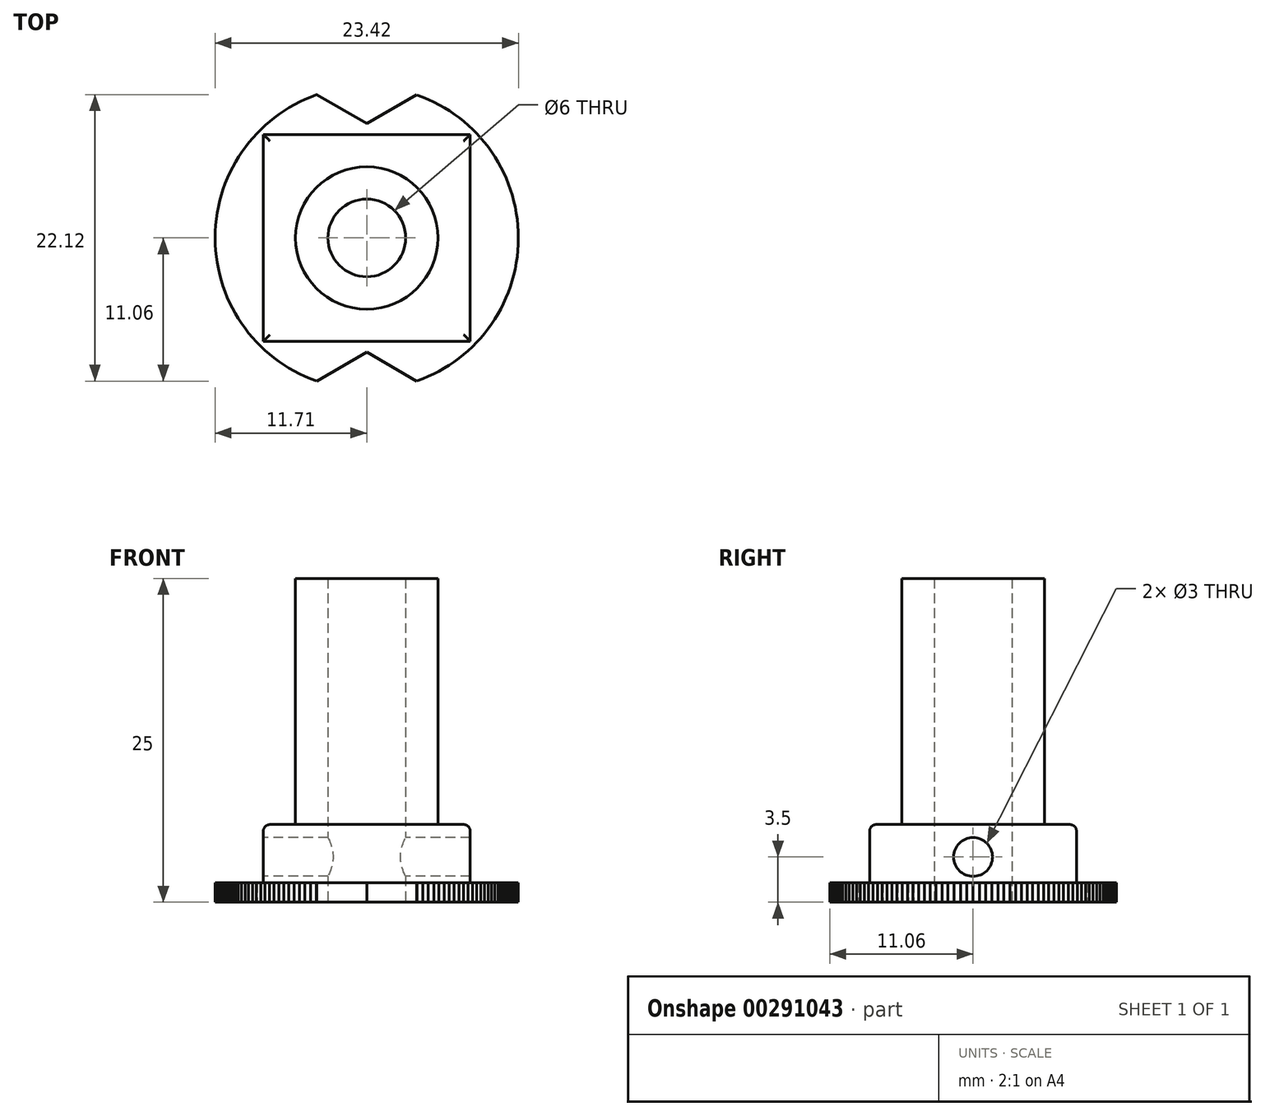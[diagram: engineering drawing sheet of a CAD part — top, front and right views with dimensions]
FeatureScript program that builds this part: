
annotation { "Feature Type Name" : "Feature", "Feature Type Description" : "" }
export const myFeature = defineFeature(function(context is Context, id is Id, definition is map)
    precondition{}
    {
        {
            var Q0;
            Q0=qCreatedBy(makeId("Top.planeOp"),FACE);
            var sketch = newSketch(context, id + "F0", { "sketchPlane" : qUnion([Q0])});
            skLineSegment(sketch, "E0", {"start": v(7.98, 7.98) * mm, "end": v(-7.98, 7.98) * mm});
            skLineSegment(sketch, "E1", {"start": v(-7.98, 7.98) * mm, "end": v(-7.98, -7.99) * mm});
            skLineSegment(sketch, "E2", {"start": v(-7.98, -7.99) * mm, "end": v(7.98, -7.99) * mm});
            skLineSegment(sketch, "E3", {"start": v(7.98, -7.99) * mm, "end": v(7.98, 7.98) * mm});
            skLineSegment(sketch, "E4", {"start": v(11.36, 2.84) * mm, "end": v(11.24, 3.3) * mm});
            skLineSegment(sketch, "E5", {"start": v(11.24, 3.3) * mm, "end": v(11.1, 3.74) * mm});
            skLineSegment(sketch, "E6", {"start": v(11.1, 3.74) * mm, "end": v(10.94, 4.17) * mm});
            skLineSegment(sketch, "E7", {"start": v(10.94, 4.17) * mm, "end": v(10.77, 4.6) * mm});
            skLineSegment(sketch, "E8", {"start": v(10.77, 4.6) * mm, "end": v(10.58, 5.02) * mm});
            skLineSegment(sketch, "E9", {"start": v(10.58, 5.02) * mm, "end": v(10.37, 5.44) * mm});
            skLineSegment(sketch, "E10", {"start": v(10.37, 5.44) * mm, "end": v(10.15, 5.84) * mm});
            skLineSegment(sketch, "E11", {"start": v(10.15, 5.84) * mm, "end": v(9.91, 6.23) * mm});
            skLineSegment(sketch, "E12", {"start": v(9.91, 6.23) * mm, "end": v(9.66, 6.62) * mm});
            skLineSegment(sketch, "E13", {"start": v(9.66, 6.62) * mm, "end": v(9.4, 6.99) * mm});
            skLineSegment(sketch, "E14", {"start": v(9.4, 6.99) * mm, "end": v(9.11, 7.35) * mm});
            skLineSegment(sketch, "E15", {"start": v(9.11, 7.35) * mm, "end": v(8.82, 7.7) * mm});
            skLineSegment(sketch, "E16", {"start": v(8.82, 7.7) * mm, "end": v(8.5, 8.04) * mm});
            skLineSegment(sketch, "E17", {"start": v(8.5, 8.04) * mm, "end": v(8.19, 8.37) * mm});
            skLineSegment(sketch, "E18", {"start": v(8.19, 8.37) * mm, "end": v(7.85, 8.68) * mm});
            skLineSegment(sketch, "E19", {"start": v(7.85, 8.68) * mm, "end": v(7.5, 8.98) * mm});
            skLineSegment(sketch, "E20", {"start": v(7.5, 8.98) * mm, "end": v(7.15, 9.27) * mm});
            skLineSegment(sketch, "E21", {"start": v(7.15, 9.27) * mm, "end": v(6.78, 9.55) * mm});
            skLineSegment(sketch, "E22", {"start": v(6.78, 9.55) * mm, "end": v(6.4, 9.8) * mm});
            skLineSegment(sketch, "E23", {"start": v(6.4, 9.8) * mm, "end": v(6, 10.05) * mm});
            skLineSegment(sketch, "E24", {"start": v(6, 10.05) * mm, "end": v(5.6, 10.28) * mm});
            skLineSegment(sketch, "E25", {"start": v(5.6, 10.28) * mm, "end": v(5.2, 10.5) * mm});
            skLineSegment(sketch, "E26", {"start": v(5.2, 10.5) * mm, "end": v(4.77, 10.7) * mm});
            skLineSegment(sketch, "E27", {"start": v(4.77, 10.7) * mm, "end": v(4.34, 10.88) * mm});
            skLineSegment(sketch, "E28", {"start": v(4.34, 10.88) * mm, "end": v(3.9, 11.04) * mm});
            skLineSegment(sketch, "E29", {"start": v(3.9, 11.04) * mm, "end": v(3.85, 11.06) * mm});
            skLineSegment(sketch, "E30", {"start": v(3.85, 11.06) * mm, "end": v(0, 8.83) * mm});
            skLineSegment(sketch, "E31", {"start": v(0, 8.83) * mm, "end": v(-3.85, 11.06) * mm});
            skLineSegment(sketch, "E32", {"start": v(-3.85, 11.06) * mm, "end": v(-3.89, 11.04) * mm});
            skLineSegment(sketch, "E33", {"start": v(-3.89, 11.04) * mm, "end": v(-4.32, 10.88) * mm});
            skLineSegment(sketch, "E34", {"start": v(-4.32, 10.88) * mm, "end": v(-4.75, 10.7) * mm});
            skLineSegment(sketch, "E35", {"start": v(-4.75, 10.7) * mm, "end": v(-5.17, 10.5) * mm});
            skLineSegment(sketch, "E36", {"start": v(-5.17, 10.5) * mm, "end": v(-5.58, 10.3) * mm});
            skLineSegment(sketch, "E37", {"start": v(-5.58, 10.3) * mm, "end": v(-5.98, 10.06) * mm});
            skLineSegment(sketch, "E38", {"start": v(-5.98, 10.06) * mm, "end": v(-6.37, 9.82) * mm});
            skLineSegment(sketch, "E39", {"start": v(-6.37, 9.82) * mm, "end": v(-6.75, 9.56) * mm});
            skLineSegment(sketch, "E40", {"start": v(-6.75, 9.56) * mm, "end": v(-7.12, 9.3) * mm});
            skLineSegment(sketch, "E41", {"start": v(-7.12, 9.3) * mm, "end": v(-7.48, 9) * mm});
            skLineSegment(sketch, "E42", {"start": v(-7.48, 9) * mm, "end": v(-7.83, 8.7) * mm});
            skLineSegment(sketch, "E43", {"start": v(-7.83, 8.7) * mm, "end": v(-8.16, 8.4) * mm});
            skLineSegment(sketch, "E44", {"start": v(-8.16, 8.4) * mm, "end": v(-8.48, 8.07) * mm});
            skLineSegment(sketch, "E45", {"start": v(-8.48, 8.07) * mm, "end": v(-8.8, 7.73) * mm});
            skLineSegment(sketch, "E46", {"start": v(-8.8, 7.73) * mm, "end": v(-9.09, 7.38) * mm});
            skLineSegment(sketch, "E47", {"start": v(-9.09, 7.38) * mm, "end": v(-9.37, 7.02) * mm});
            skLineSegment(sketch, "E48", {"start": v(-9.37, 7.02) * mm, "end": v(-9.64, 6.65) * mm});
            skLineSegment(sketch, "E49", {"start": v(-9.64, 6.65) * mm, "end": v(-9.9, 6.26) * mm});
            skLineSegment(sketch, "E50", {"start": v(-9.9, 6.26) * mm, "end": v(-10.13, 5.87) * mm});
            skLineSegment(sketch, "E51", {"start": v(-10.13, 5.87) * mm, "end": v(-10.35, 5.47) * mm});
            skLineSegment(sketch, "E52", {"start": v(-10.35, 5.47) * mm, "end": v(-10.56, 5.06) * mm});
            skLineSegment(sketch, "E53", {"start": v(-10.56, 5.06) * mm, "end": v(-10.75, 4.63) * mm});
            skLineSegment(sketch, "E54", {"start": v(-10.75, 4.63) * mm, "end": v(-10.93, 4.2) * mm});
            skLineSegment(sketch, "E55", {"start": v(-10.93, 4.2) * mm, "end": v(-11.09, 3.76) * mm});
            skLineSegment(sketch, "E56", {"start": v(-11.09, 3.76) * mm, "end": v(-11.23, 3.32) * mm});
            skLineSegment(sketch, "E57", {"start": v(-11.23, 3.32) * mm, "end": v(-11.35, 2.86) * mm});
            skLineSegment(sketch, "E58", {"start": v(-11.35, 2.86) * mm, "end": v(-11.46, 2.4) * mm});
            skLineSegment(sketch, "E59", {"start": v(-11.46, 2.4) * mm, "end": v(-11.55, 1.93) * mm});
            skLineSegment(sketch, "E60", {"start": v(-11.55, 1.93) * mm, "end": v(-11.62, 1.46) * mm});
            skLineSegment(sketch, "E61", {"start": v(-11.62, 1.46) * mm, "end": v(-11.67, 0.98) * mm});
            skLineSegment(sketch, "E62", {"start": v(-11.67, 0.98) * mm, "end": v(-11.7, 0.5) * mm});
            skLineSegment(sketch, "E63", {"start": v(-11.7, 0.5) * mm, "end": v(-11.7, 0) * mm});
            skLineSegment(sketch, "E64", {"start": v(-11.7, 0) * mm, "end": v(-11.7, -0.48) * mm});
            skLineSegment(sketch, "E65", {"start": v(-11.7, -0.48) * mm, "end": v(-11.67, -0.96) * mm});
            skLineSegment(sketch, "E66", {"start": v(-11.67, -0.96) * mm, "end": v(-11.62, -1.44) * mm});
            skLineSegment(sketch, "E67", {"start": v(-11.62, -1.44) * mm, "end": v(-11.55, -1.9) * mm});
            skLineSegment(sketch, "E68", {"start": v(-11.55, -1.9) * mm, "end": v(-11.47, -2.37) * mm});
            skLineSegment(sketch, "E69", {"start": v(-11.47, -2.37) * mm, "end": v(-11.36, -2.83) * mm});
            skLineSegment(sketch, "E70", {"start": v(-11.36, -2.83) * mm, "end": v(-11.24, -3.28) * mm});
            skLineSegment(sketch, "E71", {"start": v(-11.24, -3.28) * mm, "end": v(-11.1, -3.72) * mm});
            skLineSegment(sketch, "E72", {"start": v(-11.1, -3.72) * mm, "end": v(-10.94, -4.16) * mm});
            skLineSegment(sketch, "E73", {"start": v(-10.94, -4.16) * mm, "end": v(-10.77, -4.6) * mm});
            skLineSegment(sketch, "E74", {"start": v(-10.77, -4.6) * mm, "end": v(-10.58, -5.01) * mm});
            skLineSegment(sketch, "E75", {"start": v(-10.58, -5.01) * mm, "end": v(-10.38, -5.42) * mm});
            skLineSegment(sketch, "E76", {"start": v(-10.38, -5.42) * mm, "end": v(-10.15, -5.83) * mm});
            skLineSegment(sketch, "E77", {"start": v(-10.15, -5.83) * mm, "end": v(-9.92, -6.22) * mm});
            skLineSegment(sketch, "E78", {"start": v(-9.92, -6.22) * mm, "end": v(-9.67, -6.6) * mm});
            skLineSegment(sketch, "E79", {"start": v(-9.67, -6.6) * mm, "end": v(-9.4, -6.98) * mm});
            skLineSegment(sketch, "E80", {"start": v(-9.4, -6.98) * mm, "end": v(-9.12, -7.34) * mm});
            skLineSegment(sketch, "E81", {"start": v(-9.12, -7.34) * mm, "end": v(-8.83, -7.7) * mm});
            skLineSegment(sketch, "E82", {"start": v(-8.83, -7.7) * mm, "end": v(-8.52, -8.03) * mm});
            skLineSegment(sketch, "E83", {"start": v(-8.52, -8.03) * mm, "end": v(-8.2, -8.36) * mm});
            skLineSegment(sketch, "E84", {"start": v(-8.2, -8.36) * mm, "end": v(-7.86, -8.67) * mm});
            skLineSegment(sketch, "E85", {"start": v(-7.86, -8.67) * mm, "end": v(-7.52, -8.98) * mm});
            skLineSegment(sketch, "E86", {"start": v(-7.52, -8.98) * mm, "end": v(-7.16, -9.27) * mm});
            skLineSegment(sketch, "E87", {"start": v(-7.16, -9.27) * mm, "end": v(-6.79, -9.54) * mm});
            skLineSegment(sketch, "E88", {"start": v(-6.79, -9.54) * mm, "end": v(-6.4, -9.8) * mm});
            skLineSegment(sketch, "E89", {"start": v(-6.4, -9.8) * mm, "end": v(-6.01, -10.05) * mm});
            skLineSegment(sketch, "E90", {"start": v(-6.01, -10.05) * mm, "end": v(-5.6, -10.28) * mm});
            skLineSegment(sketch, "E91", {"start": v(-5.6, -10.28) * mm, "end": v(-5.2, -10.5) * mm});
            skLineSegment(sketch, "E92", {"start": v(-5.2, -10.5) * mm, "end": v(-4.77, -10.7) * mm});
            skLineSegment(sketch, "E93", {"start": v(-4.77, -10.7) * mm, "end": v(-4.34, -10.87) * mm});
            skLineSegment(sketch, "E94", {"start": v(-4.34, -10.87) * mm, "end": v(-3.9, -11.04) * mm});
            skLineSegment(sketch, "E95", {"start": v(-3.9, -11.04) * mm, "end": v(-3.85, -11.06) * mm});
            skLineSegment(sketch, "E96", {"start": v(-3.85, -11.06) * mm, "end": v(0, -8.83) * mm});
            skLineSegment(sketch, "E97", {"start": v(0, -8.83) * mm, "end": v(3.85, -11.06) * mm});
            skLineSegment(sketch, "E98", {"start": v(3.85, -11.06) * mm, "end": v(3.89, -11.04) * mm});
            skLineSegment(sketch, "E99", {"start": v(3.89, -11.04) * mm, "end": v(4.32, -10.88) * mm});
            skLineSegment(sketch, "E100", {"start": v(4.32, -10.88) * mm, "end": v(4.75, -10.7) * mm});
            skLineSegment(sketch, "E101", {"start": v(4.75, -10.7) * mm, "end": v(5.17, -10.5) * mm});
            skLineSegment(sketch, "E102", {"start": v(5.17, -10.5) * mm, "end": v(5.58, -10.3) * mm});
            skLineSegment(sketch, "E103", {"start": v(5.58, -10.3) * mm, "end": v(5.98, -10.06) * mm});
            skLineSegment(sketch, "E104", {"start": v(5.98, -10.06) * mm, "end": v(6.37, -9.82) * mm});
            skLineSegment(sketch, "E105", {"start": v(6.37, -9.82) * mm, "end": v(6.75, -9.56) * mm});
            skLineSegment(sketch, "E106", {"start": v(6.75, -9.56) * mm, "end": v(7.12, -9.3) * mm});
            skLineSegment(sketch, "E107", {"start": v(7.12, -9.3) * mm, "end": v(7.48, -9) * mm});
            skLineSegment(sketch, "E108", {"start": v(7.48, -9) * mm, "end": v(7.83, -8.7) * mm});
            skLineSegment(sketch, "E109", {"start": v(7.83, -8.7) * mm, "end": v(8.16, -8.4) * mm});
            skLineSegment(sketch, "E110", {"start": v(8.16, -8.4) * mm, "end": v(8.48, -8.07) * mm});
            skLineSegment(sketch, "E111", {"start": v(8.48, -8.07) * mm, "end": v(8.8, -7.73) * mm});
            skLineSegment(sketch, "E112", {"start": v(8.8, -7.73) * mm, "end": v(9.09, -7.38) * mm});
            skLineSegment(sketch, "E113", {"start": v(9.09, -7.38) * mm, "end": v(9.37, -7.02) * mm});
            skLineSegment(sketch, "E114", {"start": v(9.37, -7.02) * mm, "end": v(9.64, -6.65) * mm});
            skLineSegment(sketch, "E115", {"start": v(9.64, -6.65) * mm, "end": v(9.9, -6.26) * mm});
            skLineSegment(sketch, "E116", {"start": v(9.9, -6.26) * mm, "end": v(10.13, -5.87) * mm});
            skLineSegment(sketch, "E117", {"start": v(10.13, -5.87) * mm, "end": v(10.35, -5.47) * mm});
            skLineSegment(sketch, "E118", {"start": v(10.35, -5.47) * mm, "end": v(10.56, -5.06) * mm});
            skLineSegment(sketch, "E119", {"start": v(10.56, -5.06) * mm, "end": v(10.75, -4.63) * mm});
            skLineSegment(sketch, "E120", {"start": v(10.75, -4.63) * mm, "end": v(10.93, -4.2) * mm});
            skLineSegment(sketch, "E121", {"start": v(10.93, -4.2) * mm, "end": v(11.09, -3.76) * mm});
            skLineSegment(sketch, "E122", {"start": v(11.09, -3.76) * mm, "end": v(11.23, -3.32) * mm});
            skLineSegment(sketch, "E123", {"start": v(11.23, -3.32) * mm, "end": v(11.35, -2.86) * mm});
            skLineSegment(sketch, "E124", {"start": v(11.35, -2.86) * mm, "end": v(11.46, -2.4) * mm});
            skLineSegment(sketch, "E125", {"start": v(11.46, -2.4) * mm, "end": v(11.55, -1.93) * mm});
            skLineSegment(sketch, "E126", {"start": v(11.55, -1.93) * mm, "end": v(11.62, -1.46) * mm});
            skLineSegment(sketch, "E127", {"start": v(11.62, -1.46) * mm, "end": v(11.67, -0.98) * mm});
            skLineSegment(sketch, "E128", {"start": v(11.67, -0.98) * mm, "end": v(11.7, -0.5) * mm});
            skLineSegment(sketch, "E129", {"start": v(11.7, -0.5) * mm, "end": v(11.7, 0) * mm});
            skLineSegment(sketch, "E130", {"start": v(11.7, 0) * mm, "end": v(11.7, 0.49) * mm});
            skLineSegment(sketch, "E131", {"start": v(11.7, 0.49) * mm, "end": v(11.67, 0.97) * mm});
            skLineSegment(sketch, "E132", {"start": v(11.67, 0.97) * mm, "end": v(11.62, 1.44) * mm});
            skLineSegment(sketch, "E133", {"start": v(11.62, 1.44) * mm, "end": v(11.55, 1.91) * mm});
            skLineSegment(sketch, "E134", {"start": v(11.55, 1.91) * mm, "end": v(11.46, 2.38) * mm});
            skLineSegment(sketch, "E135", {"start": v(11.46, 2.38) * mm, "end": v(11.36, 2.84) * mm});
            skArc(sketch, "E136", {"start": v(0, 3) * mm, "mid": v(-2.12, 2.12) * mm, "end": v(-3, 0) * mm});
            skArc(sketch, "E137", {"start": v(-3, 0) * mm, "mid": v(-2.12, -2.12) * mm, "end": v(0, -3) * mm});
            skArc(sketch, "E138", {"start": v(0, -3) * mm, "mid": v(2.12, -2.12) * mm, "end": v(3, 0) * mm});
            skArc(sketch, "E139", {"start": v(3, 0) * mm, "mid": v(2.12, 2.12) * mm, "end": v(0, 3) * mm});
            skArc(sketch, "E140", {"start": v(0, 5.5) * mm, "mid": v(-3.89, 3.89) * mm, "end": v(-5.5, 0) * mm});
            skArc(sketch, "E141", {"start": v(-5.5, 0) * mm, "mid": v(-3.89, -3.89) * mm, "end": v(0, -5.5) * mm});
            skArc(sketch, "E142", {"start": v(0, -5.5) * mm, "mid": v(3.89, -3.89) * mm, "end": v(5.5, 0) * mm});
            skArc(sketch, "E143", {"start": v(5.5, 0) * mm, "mid": v(3.89, 3.89) * mm, "end": v(0, 5.5) * mm});
            skSolve(sketch);
        }
        {
            var Q0;
            Q0=makeQuery(id+"F0.imprint","IMPRINT",FACE,{"disambiguationData":[TD([[makeQuery(id+"F0.imprint","IMPRINT",EDGE,{"derivedFrom":sQuery(id+"F0.wireOp",EDGE,"E0")}),-1.0]])]});
            extrude(context, id + "F1", {"entities" : qUnion([Q0]), "depth" : 1.5 * mm});
        }
        {
            var Q0;
            Q0=makeQuery(id+"F0.imprint","IMPRINT",FACE,{"disambiguationData":[TD([[makeQuery(id+"F0.imprint","IMPRINT",EDGE,{"derivedFrom":sQuery(id+"F0.wireOp",EDGE,"E0")}),1.0]])]});
            extrude(context, id + "F2", {"entities" : qUnion([Q0]), "operationType" : NewBodyOperationType.ADD, "depth" : 6 * mm});
        }
        {
            var Q0;
            Q0=makeQuery(id+"F0.imprint","IMPRINT",FACE,{"disambiguationData":[TD([[makeQuery(id+"F0.imprint","IMPRINT",EDGE,{"derivedFrom":sQuery(id+"F0.wireOp",EDGE,"E136")}),-1.0]])]});
            extrude(context, id + "F3", {"entities" : qUnion([Q0]), "operationType" : NewBodyOperationType.ADD, "depth" : 14 * mm});
        }
        {
            var Q0;
            Q0=makeQuery(id+"F2.opExtrude","CAP_EDGE",EDGE,{"disambiguationData":[OSD([sQuery(id+"F0.wireOp",EDGE,"E1")])],"isStart":false});
            var Q1;
            Q1=makeQuery(id+"F2.opExtrude","CAP_EDGE",EDGE,{"disambiguationData":[OSD([sQuery(id+"F0.wireOp",EDGE,"E2")])],"isStart":false});
            var Q2;
            Q2=makeQuery(id+"F2.opExtrude","CAP_EDGE",EDGE,{"disambiguationData":[OSD([sQuery(id+"F0.wireOp",EDGE,"E3")])],"isStart":false});
            var Q3;
            Q3=makeQuery(id+"F2.opExtrude","CAP_EDGE",EDGE,{"disambiguationData":[OSD([sQuery(id+"F0.wireOp",EDGE,"E0")])],"isStart":false});
            fillet(context, id + "F4", {"entities" : qUnion([Q0, Q1, Q2, Q3]), "radius" : 0.5 * mm, "tangentPropagation" : true, "allowEdgeOverflow" : false});
        }
        {
            var Q0;
            Q0=makeQuery(id+"F0.imprint","IMPRINT",FACE,{"disambiguationData":[TD([[makeQuery(id+"F0.imprint","IMPRINT",EDGE,{"derivedFrom":sQuery(id+"F0.wireOp",EDGE,"E136")}),-1.0]])]});
            extrude(context, id + "F5", {"entities" : qUnion([Q0]), "operationType" : NewBodyOperationType.ADD, "depth" : 25 * mm});
        }
        {
            var Q0;
            Q0=makeQuery(id+"F2.opExtrude","SWEPT_FACE",FACE,{"disambiguationData":[OSD([sQuery(id+"F0.wireOp",EDGE,"E1")])]});
            var sketch = newSketch(context, id + "F6", { "sketchPlane" : qUnion([Q0])});
            skLineSegment(sketch, "E144", {"start": v(0, 1.5) * mm, "end": v(0, 5.5) * mm});
            skLineSegment(sketch, "E145", {"start": v(0, 5.5) * mm, "end": v(0, 3.5) * mm});
            skLineSegment(sketch, "E146", {"start": v(0, 3.5) * mm, "end": v(-1.34, 3.5) * mm});
            skSolve(sketch);
        }
        {
            var Q0;
            Q0=sQuery(id+"F6.wireOp",VERTEX,"E146.start");
            var Q1;
            Q1=makeQuery(id+"F1.opExtrude","SWEPT_BODY",BODY,{"disambiguationData":[OSD([sQuery(id+"F0.wireOp",EDGE,"E0"),sQuery(id+"F0.wireOp",EDGE,"E1"),sQuery(id+"F0.wireOp",EDGE,"E2"),sQuery(id+"F0.wireOp",EDGE,"E3"),sQuery(id+"F0.wireOp",EDGE,"E4"),sQuery(id+"F0.wireOp",EDGE,"E5"),sQuery(id+"F0.wireOp",EDGE,"E6"),sQuery(id+"F0.wireOp",EDGE,"E7"),sQuery(id+"F0.wireOp",EDGE,"E8"),sQuery(id+"F0.wireOp",EDGE,"E9"),sQuery(id+"F0.wireOp",EDGE,"E10"),sQuery(id+"F0.wireOp",EDGE,"E11"),sQuery(id+"F0.wireOp",EDGE,"E12"),sQuery(id+"F0.wireOp",EDGE,"E13"),sQuery(id+"F0.wireOp",EDGE,"E14"),sQuery(id+"F0.wireOp",EDGE,"E15"),sQuery(id+"F0.wireOp",EDGE,"E16"),sQuery(id+"F0.wireOp",EDGE,"E17"),sQuery(id+"F0.wireOp",EDGE,"E18"),sQuery(id+"F0.wireOp",EDGE,"E19"),sQuery(id+"F0.wireOp",EDGE,"E20"),sQuery(id+"F0.wireOp",EDGE,"E21"),sQuery(id+"F0.wireOp",EDGE,"E22"),sQuery(id+"F0.wireOp",EDGE,"E23"),sQuery(id+"F0.wireOp",EDGE,"E24"),sQuery(id+"F0.wireOp",EDGE,"E25"),sQuery(id+"F0.wireOp",EDGE,"E26"),sQuery(id+"F0.wireOp",EDGE,"E27"),sQuery(id+"F0.wireOp",EDGE,"E28"),sQuery(id+"F0.wireOp",EDGE,"E29"),sQuery(id+"F0.wireOp",EDGE,"E30"),sQuery(id+"F0.wireOp",EDGE,"E31"),sQuery(id+"F0.wireOp",EDGE,"E32"),sQuery(id+"F0.wireOp",EDGE,"E33"),sQuery(id+"F0.wireOp",EDGE,"E34"),sQuery(id+"F0.wireOp",EDGE,"E35"),sQuery(id+"F0.wireOp",EDGE,"E36"),sQuery(id+"F0.wireOp",EDGE,"E37"),sQuery(id+"F0.wireOp",EDGE,"E38"),sQuery(id+"F0.wireOp",EDGE,"E39"),sQuery(id+"F0.wireOp",EDGE,"E40"),sQuery(id+"F0.wireOp",EDGE,"E41"),sQuery(id+"F0.wireOp",EDGE,"E42"),sQuery(id+"F0.wireOp",EDGE,"E43"),sQuery(id+"F0.wireOp",EDGE,"E44"),sQuery(id+"F0.wireOp",EDGE,"E45"),sQuery(id+"F0.wireOp",EDGE,"E46"),sQuery(id+"F0.wireOp",EDGE,"E47"),sQuery(id+"F0.wireOp",EDGE,"E48"),sQuery(id+"F0.wireOp",EDGE,"E49"),sQuery(id+"F0.wireOp",EDGE,"E50"),sQuery(id+"F0.wireOp",EDGE,"E51"),sQuery(id+"F0.wireOp",EDGE,"E52"),sQuery(id+"F0.wireOp",EDGE,"E53"),sQuery(id+"F0.wireOp",EDGE,"E54"),sQuery(id+"F0.wireOp",EDGE,"E55"),sQuery(id+"F0.wireOp",EDGE,"E56"),sQuery(id+"F0.wireOp",EDGE,"E57"),sQuery(id+"F0.wireOp",EDGE,"E58"),sQuery(id+"F0.wireOp",EDGE,"E59"),sQuery(id+"F0.wireOp",EDGE,"E60"),sQuery(id+"F0.wireOp",EDGE,"E61"),sQuery(id+"F0.wireOp",EDGE,"E62"),sQuery(id+"F0.wireOp",EDGE,"E63"),sQuery(id+"F0.wireOp",EDGE,"E64"),sQuery(id+"F0.wireOp",EDGE,"E65"),sQuery(id+"F0.wireOp",EDGE,"E66"),sQuery(id+"F0.wireOp",EDGE,"E67"),sQuery(id+"F0.wireOp",EDGE,"E68"),sQuery(id+"F0.wireOp",EDGE,"E69"),sQuery(id+"F0.wireOp",EDGE,"E70"),sQuery(id+"F0.wireOp",EDGE,"E71"),sQuery(id+"F0.wireOp",EDGE,"E72"),sQuery(id+"F0.wireOp",EDGE,"E73"),sQuery(id+"F0.wireOp",EDGE,"E74"),sQuery(id+"F0.wireOp",EDGE,"E75"),sQuery(id+"F0.wireOp",EDGE,"E76"),sQuery(id+"F0.wireOp",EDGE,"E77"),sQuery(id+"F0.wireOp",EDGE,"E78"),sQuery(id+"F0.wireOp",EDGE,"E79"),sQuery(id+"F0.wireOp",EDGE,"E80"),sQuery(id+"F0.wireOp",EDGE,"E81"),sQuery(id+"F0.wireOp",EDGE,"E82"),sQuery(id+"F0.wireOp",EDGE,"E83"),sQuery(id+"F0.wireOp",EDGE,"E84"),sQuery(id+"F0.wireOp",EDGE,"E85"),sQuery(id+"F0.wireOp",EDGE,"E86"),sQuery(id+"F0.wireOp",EDGE,"E87"),sQuery(id+"F0.wireOp",EDGE,"E88"),sQuery(id+"F0.wireOp",EDGE,"E89"),sQuery(id+"F0.wireOp",EDGE,"E90"),sQuery(id+"F0.wireOp",EDGE,"E91"),sQuery(id+"F0.wireOp",EDGE,"E92"),sQuery(id+"F0.wireOp",EDGE,"E93"),sQuery(id+"F0.wireOp",EDGE,"E94"),sQuery(id+"F0.wireOp",EDGE,"E95"),sQuery(id+"F0.wireOp",EDGE,"E96"),sQuery(id+"F0.wireOp",EDGE,"E97"),sQuery(id+"F0.wireOp",EDGE,"E98"),sQuery(id+"F0.wireOp",EDGE,"E99"),sQuery(id+"F0.wireOp",EDGE,"E100"),sQuery(id+"F0.wireOp",EDGE,"E101"),sQuery(id+"F0.wireOp",EDGE,"E102"),sQuery(id+"F0.wireOp",EDGE,"E103"),sQuery(id+"F0.wireOp",EDGE,"E104"),sQuery(id+"F0.wireOp",EDGE,"E105"),sQuery(id+"F0.wireOp",EDGE,"E106"),sQuery(id+"F0.wireOp",EDGE,"E107"),sQuery(id+"F0.wireOp",EDGE,"E108"),sQuery(id+"F0.wireOp",EDGE,"E109"),sQuery(id+"F0.wireOp",EDGE,"E110"),sQuery(id+"F0.wireOp",EDGE,"E111"),sQuery(id+"F0.wireOp",EDGE,"E112"),sQuery(id+"F0.wireOp",EDGE,"E113"),sQuery(id+"F0.wireOp",EDGE,"E114"),sQuery(id+"F0.wireOp",EDGE,"E115"),sQuery(id+"F0.wireOp",EDGE,"E116"),sQuery(id+"F0.wireOp",EDGE,"E117"),sQuery(id+"F0.wireOp",EDGE,"E118"),sQuery(id+"F0.wireOp",EDGE,"E119"),sQuery(id+"F0.wireOp",EDGE,"E120"),sQuery(id+"F0.wireOp",EDGE,"E121"),sQuery(id+"F0.wireOp",EDGE,"E122"),sQuery(id+"F0.wireOp",EDGE,"E123"),sQuery(id+"F0.wireOp",EDGE,"E124"),sQuery(id+"F0.wireOp",EDGE,"E125"),sQuery(id+"F0.wireOp",EDGE,"E126"),sQuery(id+"F0.wireOp",EDGE,"E127"),sQuery(id+"F0.wireOp",EDGE,"E128"),sQuery(id+"F0.wireOp",EDGE,"E129"),sQuery(id+"F0.wireOp",EDGE,"E130"),sQuery(id+"F0.wireOp",EDGE,"E131"),sQuery(id+"F0.wireOp",EDGE,"E132"),sQuery(id+"F0.wireOp",EDGE,"E133"),sQuery(id+"F0.wireOp",EDGE,"E134"),sQuery(id+"F0.wireOp",EDGE,"E135")])]});
            hole(context, id + "F7", {"style" : HoleStyle.SIMPLE, "endStyle" : HoleEndStyle.THROUGH, "holeDiameter" : 3 * mm, "tappedDepth" : 12 * mm, "tapClearance" : 3, "locations" : qUnion([Q0]), "scope" : qUnion([Q1])});
        }
    });
